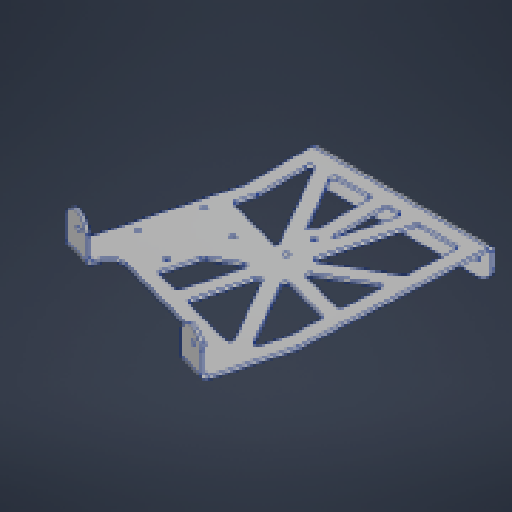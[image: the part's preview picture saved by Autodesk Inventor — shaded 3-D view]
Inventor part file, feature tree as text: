
AUTODESK INVENTOR PART (.ipt)
format: ipt  version: 2024.3 (Build 283343010, 343A)  size: 430,080 bytes
history: native  units: in
note: dims shown in document units (in); Inventor stores cm internally (conversion verified against a paired STEP export)
features: sheet_metal_op x14, sketch x13, other x11, projected_geometry x5, hole x4, chamfer x3, plane x2, extrude x1
ambient origin geometry x8: Origin, YZ Plane, XZ Plane, XY Plane, X Axis, Y Axis, Z Axis, Center Point
bodies: Solid1 (feature_tree)
feature tree (53):
  sheet_metal_op  "Face1"
  sheet_metal_op  "Flange1"
  plane  "Work Plane1"
  sheet_metal_op  "Face2"
  sheet_metal_op  "Face4"
  sheet_metal_op  "Bend6"
  plane  "Work Plane2"
  sheet_metal_op  "Face5"
  sheet_metal_op  "Bend8"
  hole  "Hole1"  [1 undecoded]
  hole  "Hole3"  [1 undecoded]
  hole  "Hole4"  [1 undecoded]
  sheet_metal_op  "Face6"
  chamfer  "Corner Round2"
  extrude  "Extrusion1"  Depth=0.24in
  chamfer  "Corner Round3"
  chamfer  "Corner Round4"
  hole  "Hole5"  [1 undecoded]
  sketch  "Sketch1"  dims[d3=6.5in d4=0.5in]
  other  "Plate1"
  sketch  "Sketch2"  dims[d5=1.0in d7=0.5938in]
  other  "Plate2"
  sheet_metal_op  "Bend1"
  sheet_metal_op  "Corner1"
  sketch  "Sketch3"  dims[d8=0.12in d9=0.12in]
  other  "Plate3"
  sheet_metal_op  "Bend2"
  sketch  "Sketch4"  dims[d10=0.06in d11=0.24in]
  projected_geometry  "Projected Loop1"
  sketch  "Sketch6"  dims[d12=0.12in d13=7.0in d14=90.0deg d15=0.12in]
  projected_geometry  "Projected Loop4"
  other  "Plate5"
  sheet_metal_op  "Bend5"
  sketch  "Sketch7"  dims[d16=0.48in]
  other  "Plate6"
  sheet_metal_op  "Bend7"
  sketch  "Sketch8"  dims[d17=0.12in]
  projected_geometry  "Projected Loop5"
  sketch  "Sketch9"  dims[d18=0.12in]
  projected_geometry  "Projected Loop6"
  sketch  "Sketch11"  dims[d19=1.0in]
  sketch  "Sketch12"  dims[d20=0.765in]
  sketch  "Sketch13"  dims[d21=1.0in]
  other  "Plate7"
  sheet_metal_op  "Bend9"
  sketch  "Sketch14"  dims[d22=0.12in]
  projected_geometry  "Projected Loop7"
  sketch  "Sketch15"  dims[d23=0.12in d24=0.06in d25=0.24in d26=0.12in d27=165.0deg d28=0.12in d29=0.0in d42=0.12in d43=0.12in d44=0.06in d45=0.24in d46=0.12in d47=0.12in d48=0.06in d49=0.24in d50=0.12in d51=0.12in d52=1.0in d53=0.765in d54=1.0in d55=0.12in d56=0.12in d57=0.06in d58=0.24in d59=0.12in d60=0.12in d61=0.06in d62=0.24in d63=0.12in d64=0.12in d65=0.12in d66=0.0in d68=0.201in d69=0.75in d70=0.385in d71=0.25in d72=0.5635in d73=0.12in d74=0.8108in d82=1.0in d84=0.201in d85=0.75in d86=0.375in d87=0.25in d88=0.5635in d89=1.0in d90=0.8108in d91=3.0in d92=0.201in d93=0.75in d94=0.385in d95=0.25in d96=0.5635in d97=0.12in d98=0.8108in d99=2.0in d100=0.12in d101=0.12in d102=0.06in d103=0.24in d104=0.12in d105=0.5in d106=1.0in d107=0.5in d108=0.5in d109=0.5in d110=0.5in d111=0.5in d112=0.5in d113=45.0deg d114=0.5in d115=0.5in d116=45.0deg d117=0.5in d118=0.5in d119=0.5in d120=0.125in d121=0.0in d122=0.125in d123=1.5in d124=2.0in d126=1.0in d127=0.125in d128=0.375in d129=0.75in d130=0.201in d131=0.75in d132=0.375in d133=0.25in d134=0.5635in d135=1.0in d136=0.8108in d137=0.5in d138=1.0in d139=90.0deg d140=0.125in d141=0.125in]
  other  "Cut1"
  other  "Cut2"
  parser-record x1  (decoder bookkeeping rows leaked as tree rows — omitted from the tree; the rows remain in map.json)
  other  "#Poseidon 2025.iam"
  other  "feeder_bottom_plate:1"
note: 4 required parameter values undecoded (feature->parameter linkage not recoverable at this tier; creation-order binding heuristic only, values carry confidence <= 0.55)
note: 1 file-system path scrubbed to <path> (originals preserved in map.json)
